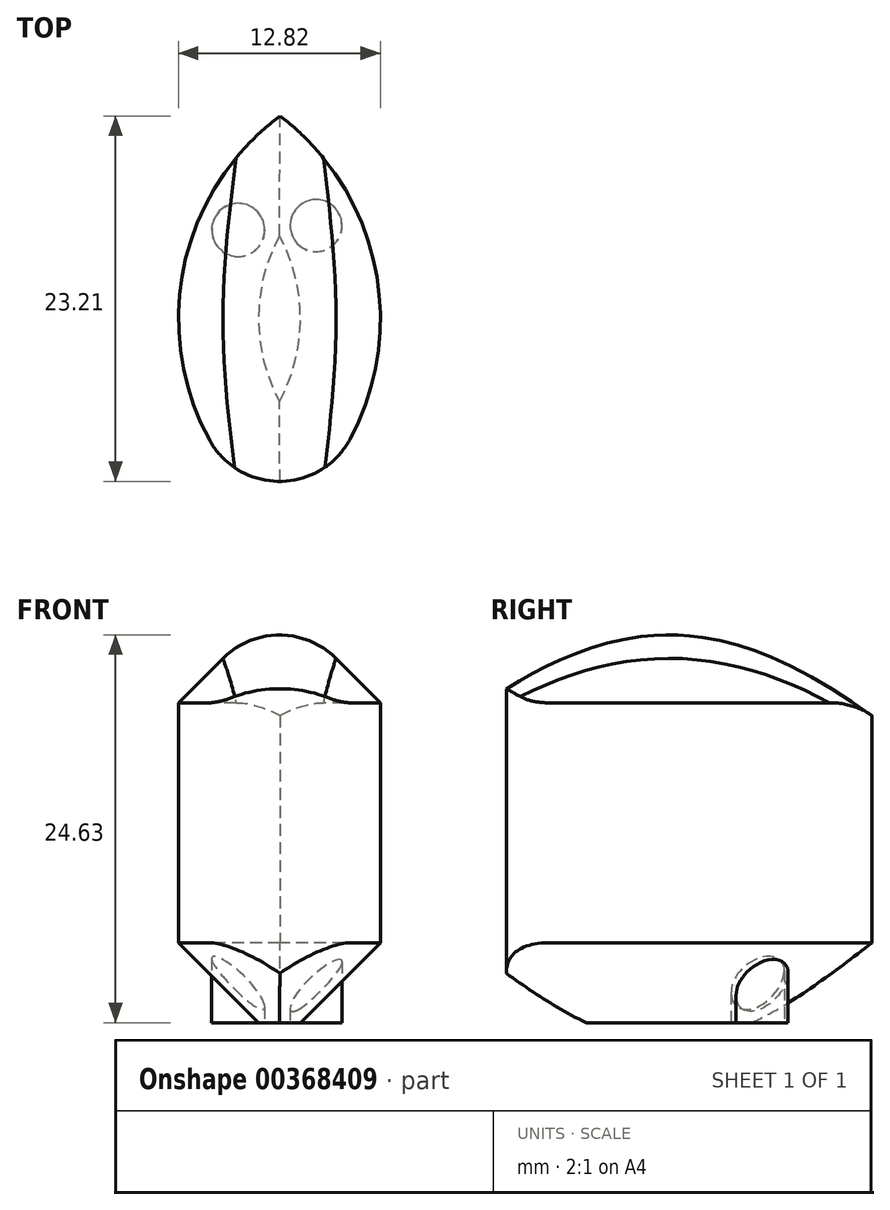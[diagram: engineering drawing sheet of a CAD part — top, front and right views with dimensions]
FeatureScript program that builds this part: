
annotation { "Feature Type Name" : "Feature", "Feature Type Description" : "" }
export const myFeature = defineFeature(function(context is Context, id is Id, definition is map)
    precondition{}
    {
        {
            var Q0;
            Q0=qCreatedBy(makeId("Top.planeOp"),FACE);
            var sketch = newSketch(context, id + "F0", { "sketchPlane" : qUnion([Q0])});
            skArc(sketch, "E0", {"start": v(0, 0) * mm, "mid": v(6.37, 12.88) * mm, "end": v(0, 25.75) * mm});
            skArc(sketch, "E1", {"start": v(0, 25.75) * mm, "mid": v(-6.45, 12.88) * mm, "end": v(0, 0) * mm});
            skLineSegment(sketch, "E2", {"start": v(0, 23) * mm, "end": v(0, 3.02) * mm});
            skArc(sketch, "E3", {"start": v(0, 25.75) * mm, "mid": v(-6.88, 28.85) * mm, "end": v(-13.3, 24.88) * mm});
            skSolve(sketch);
        }
        {
            var Q0;
            Q0=makeQuery(id+"F0.imprint","IMPRINT",FACE,{"disambiguationData":[TD([[makeQuery(id+"F0.imprint","IMPRINT",EDGE,{"derivedFrom":sQuery(id+"F0.wireOp",EDGE,"E0")}),1.0]])]});
            extrude(context, id + "F1", {"entities" : qUnion([Q0]), "depth" : 25.4 * mm});
        }
        {
            var Q0;
            Q0=makeQuery(id+"F1.opExtrude","CAP_EDGE",EDGE,{"disambiguationData":[OSD([sQuery(id+"F0.wireOp",EDGE,"E1")])],"isStart":true});
            var Q1;
            Q1=makeQuery(id+"F1.opExtrude","CAP_EDGE",EDGE,{"disambiguationData":[OSD([sQuery(id+"F0.wireOp",EDGE,"E1")])],"isStart":false});
            var Q2;
            Q2=makeQuery(id+"F1.opExtrude","CAP_EDGE",EDGE,{"disambiguationData":[OSD([sQuery(id+"F0.wireOp",EDGE,"E0")])],"isStart":false});
            var Q3;
            Q3=makeQuery(id+"F1.opExtrude","CAP_EDGE",EDGE,{"disambiguationData":[OSD([sQuery(id+"F0.wireOp",EDGE,"E0")])],"isStart":true});
            chamfer(context, id + "F2", {"entities" : qUnion([Q0, Q1, Q2, Q3]), "width" : 5.08 * mm, "tangentPropagation" : true});
        }
        {
            var Q0;
            {var subQ0=sQuery(id+"F0.wireOp",EDGE,"E1");var subQ1=sQuery(id+"F0.wireOp",EDGE,"E0");Q0=makeQuery(id+"F1.opExtrude","SWEPT_EDGE",EDGE,{"disambiguationData":[OSD([subQ1,subQ0]),TDD([makeQuery(id+"F0.imprint","INTERSECT",VERTEX,{"disambiguationData":[OD(0.0)],"derivedFrom":[subQ1,subQ0]})])]});}
            var Q1;
            Q1=makeQuery(id+"F2.opChamfer","BLEND_EDGE",EDGE,{"disambiguationData":[OD(0.0)],"blendedFrom":[makeQuery(id+"F1.opExtrude","CAP_EDGE",EDGE,{"disambiguationData":[OSD([sQuery(id+"F0.wireOp",EDGE,"E0")])],"isStart":false}),makeQuery(id+"F1.opExtrude","CAP_EDGE",EDGE,{"disambiguationData":[OSD([sQuery(id+"F0.wireOp",EDGE,"E1")])],"isStart":false})],"blendedInto":[]});
            fillet(context, id + "F3", {"entities" : qUnion([Q0, Q1]), "radius" : 5.08 * mm, "tangentPropagation" : true, "allowEdgeOverflow" : false});
        }
        {
            var Q0;
            Q0=qCreatedBy(makeId("Top.planeOp"),FACE);
            var sketch = newSketch(context, id + "F4", { "sketchPlane" : qUnion([Q0])});
            skCircle(sketch, "E4", {"center": v(2.3, 18.79) * mm, "radius": 1.65 * mm});
            skCircle(sketch, "E5", {"center": v(-2.66, 18.51) * mm, "radius": 1.69 * mm});
            skSolve(sketch);
        }
        {
            var Q0;
            Q0=makeQuery(id+"F4.imprint","IMPRINT",FACE,{"disambiguationData":[TD([[makeQuery(id+"F4.imprint","IMPRINT",EDGE,{"derivedFrom":sQuery(id+"F4.wireOp",EDGE,"E5")}),1.0]])]});
            var Q1;
            Q1=makeQuery(id+"F4.imprint","IMPRINT",FACE,{"disambiguationData":[TD([[makeQuery(id+"F4.imprint","IMPRINT",EDGE,{"derivedFrom":sQuery(id+"F4.wireOp",EDGE,"E4")}),1.0]])]});
            extrude(context, id + "F5", {"entities" : qUnion([Q0, Q1]), "operationType" : NewBodyOperationType.ADD, "depth" : 12.7 * mm});
        }
    });
